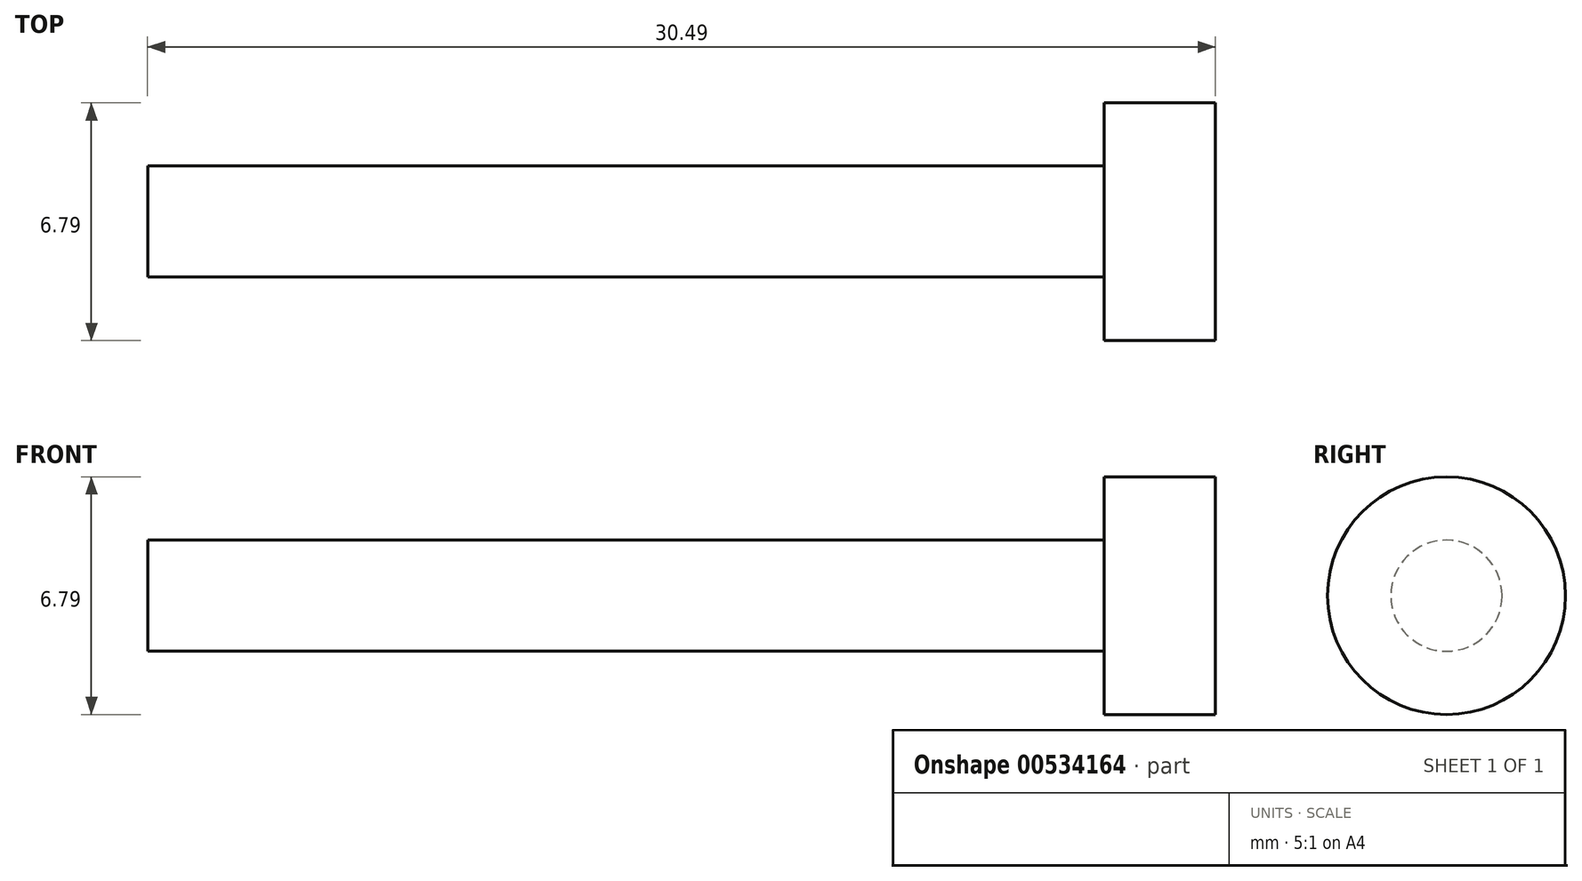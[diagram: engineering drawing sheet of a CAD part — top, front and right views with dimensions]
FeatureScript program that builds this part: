
annotation { "Feature Type Name" : "Feature", "Feature Type Description" : "" }
export const myFeature = defineFeature(function(context is Context, id is Id, definition is map)
    precondition{}
    {
        {
            var Q0;
            Q0=qCreatedBy(makeId("Right.planeOp"),FACE);
            var sketch = newSketch(context, id + "F0", { "sketchPlane" : qUnion([Q0])});
            skCircle(sketch, "E0", {"center": v(-14.2, 11.47) * mm, "radius": 1.59 * mm});
            skSolve(sketch);
        }
        {
            var Q0;
            Q0 = qSketchRegion(id + "F0", true);
            extrude(context, id + "F1", {"entities" : qUnion([Q0]), "depth" : 38.1 * mm, "offsetDistance" : 25.4 * mm});
        }
        {
            var Q0;
            Q0=makeQuery(id+"F1.opExtrude","CAP_FACE",FACE,{"disambiguationData":[OSD([sQuery(id+"F0.wireOp",EDGE,"E0")])],"isStart":false});
            var sketch = newSketch(context, id + "F2", { "sketchPlane" : qUnion([Q0])});
            skCircle(sketch, "E1", {"center": v(-14.2, 11.47) * mm, "radius": 3.4 * mm});
            skSolve(sketch);
        }
        {
            var Q0;
            Q0 = qSketchRegion(id + "F2", true);
            extrude(context, id + "F3", {"entities" : qUnion([Q0]), "operationType" : NewBodyOperationType.ADD, "depth" : 3.17 * mm, "offsetDistance" : 25.4 * mm});
        }
        {
            var Q0;
            Q0=makeQuery(id+"F1.opExtrude","CAP_FACE",FACE,{"disambiguationData":[OSD([sQuery(id+"F0.wireOp",EDGE,"E0")])],"isStart":true});
            extrude(context, id + "F4", {"entities" : qUnion([Q0]), "operationType" : NewBodyOperationType.REMOVE, "oppositeDirection" : true, "depth" : 10.8 * mm, "offsetDistance" : 25.4 * mm});
        }
    });
